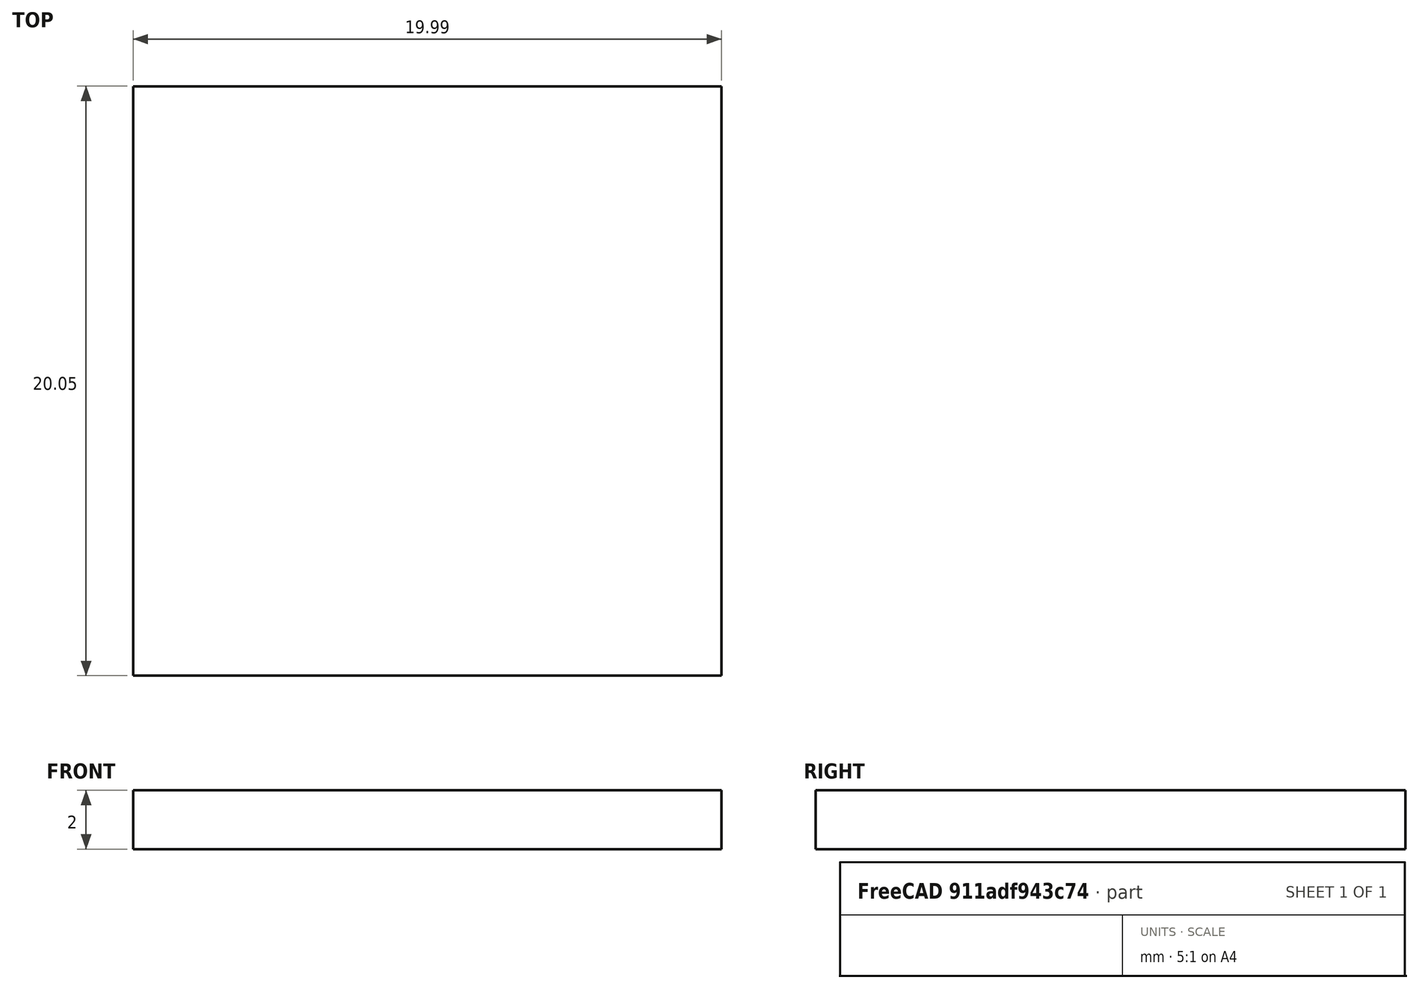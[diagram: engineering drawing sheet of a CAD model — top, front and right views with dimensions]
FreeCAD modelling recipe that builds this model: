
FCSTD DOCUMENT  (FreeCAD 0.19R)
Label: Body
License: All rights reserved
LicenseURL: http://en.wikipedia.org/wiki/All_rights_reserved
objects: App::Part×1, Sketcher::SketchObject×1, PartDesign::Pad×1, PartDesign::Body×1
note: 4 computed .brp shape members not serialized (recipe doc carries the construction recipe); baked Part::Feature solids carry a one-line shape summary decoded from their .brp

FEATURE [App::Part] Part
  Origin = -> Origin
FEATURE [Sketcher::SketchObject] Sketch
  FullyConstrained = false
  MapMode = 5
  Support = -> [XY_Plane001]
  sketch-geometry (4):
    g0: LineSegment StartX=0 StartY=0 StartZ=0 EndX=19.9877 EndY=0 EndZ=0
    g1: LineSegment StartX=19.9877 StartY=0 StartZ=0 EndX=19.9877 EndY=20.0455 EndZ=0
    g2: LineSegment StartX=19.9877 StartY=20.0455 StartZ=0 EndX=0 EndY=20.0455 EndZ=0
    g3: LineSegment StartX=0 StartY=20.0455 StartZ=0 EndX=0 EndY=0 EndZ=0
  constraints (9):
    c: Coincident(g0,g1)
    c: Coincident(g1,g2)
    c: Coincident(g2,g3)
    c: Coincident(g3,g0)
    c: Horizontal(g0)
    c: Horizontal(g2)
    c: Vertical(g1)
    c: Vertical(g3)
    c: Coincident(g0,g-1)
FEATURE [PartDesign::Pad] Pad
  Direction = (1,1,1)
  Length = 2
  Length2 = 100
  Profile = -> Sketch
  Type = 0
FEATURE [PartDesign::Body] Body
  Group = -> [Sketch,Pad]
  Origin = -> Origin001
  Tip = -> Pad
